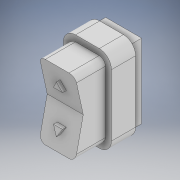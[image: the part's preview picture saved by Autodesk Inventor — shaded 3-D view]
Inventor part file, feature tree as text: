
AUTODESK INVENTOR PART (.ipt)
format: ipt  version: 2022 (Build 260153000, 153)  size: 190,464 bytes
history: native  units: in
note: dims shown in document units (in); Inventor stores cm internally (conversion verified against a paired STEP export)
features: extrude x6, sketch x6, projected_geometry x2
ambient origin geometry x8: Origin, YZ Plane, XZ Plane, XY Plane, X Axis, Y Axis, Z Axis, Center Point
bodies: Solid1 (feature_tree)
feature tree (14):
  extrude  "Extrusion1"  Depth=0.5315in TaperAngle=0.0deg
  extrude  "Extrusion2"  Depth=0.2362in TaperAngle=0.0deg
  extrude  "Extrusion3"  Depth=0.3612in TaperAngle=0.0deg
  extrude  "Extrusion4"  Depth=0.0354in
  extrude  "Extrusion5"  Depth=0.389in
  extrude  "Extrusion6"  Depth=0.1181in
  sketch  "Sketch1"  dims[d0=0.0185in d1=0.5315in d2=0.0in]
  sketch  "Sketch2"  dims[d3=0.0591in d4=0.2362in d5=0.0in]
  projected_geometry  "Projected Loop1"
  sketch  "Sketch3"  dims[d6=0.0787in d7=0.3612in d8=0.0in]
  sketch  "Sketch4"  dims[d9=0.4237in d10=0.0in d11=0.0354in]
  projected_geometry  "Projected Loop2"
  sketch  "Sketch5"  dims[d12=0.4237in d13=0.0in d14=0.389in]
  sketch  "Sketch6"  dims[d15=0.7614in d16=0.0185in d17=0.1181in d18=0.0in]
